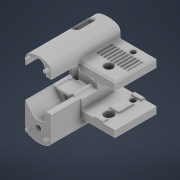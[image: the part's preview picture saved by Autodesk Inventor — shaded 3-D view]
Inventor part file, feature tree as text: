
AUTODESK INVENTOR PART (.ipt)
format: ipt  version: 2022.1 (Build 261234000, 234)  size: 1,596,416 bytes
history: native  units: mm
features: projected_geometry x43, extrude x31, sketch x31, reference x20, chamfer x19, other x11, move_body x11, direct_edit x8, fillet x7, hole x5, plane x4, delete_face x4, mirror x1
ambient origin geometry x8: Origin, YZ Plane, XZ Plane, XY Plane, X Axis, Y Axis, Z Axis, Center Point
bodies: Volumenkörper1 (feature_tree)
feature tree (195):
  extrude  "Extrusion1"  Depth=20.0mm
  extrude  "Extrusion2"  Depth=25.0mm
  plane  "Arbeitsebene1"
  extrude  "Extrusion5"  Depth=20.0mm
  sketch  "Skizze5"  dims[d7=20.0mm d8=10.0mm]
  extrude  "Extrusion6"  Depth=10.0mm
  hole  "Bohrung1"  [1 undecoded]
  extrude  "Extrusion10"  Depth=7.1mm
  sketch  "Skizze10"  dims[d28=15.0mm d29=17.0mm]
  hole  "Bohrung2"  [1 undecoded]
  hole  "Bohrung3"  [1 undecoded]
  extrude  "Extrusion11"  Depth=0.1mm
  extrude  "Extrusion12"  Depth=7.1mm
  direct_edit  "Direktbearbeitung3"
  direct_edit  "Direktbearbeitung4"
  extrude  "Extrusion13"  Depth=7.1mm
  fillet  "Rundung6"  Radius=18.2mm
  direct_edit  "Direktbearbeitung5"
  extrude  "Extrusion14"  Depth=11.0mm TaperAngle=0.0deg
  chamfer  "Fase2"  [1 undecoded]
  chamfer  "Fase3"  [1 undecoded]
  hole  "Bohrung5"  [1 undecoded]
  extrude  "Extrusion18"  Depth=4.0mm TaperAngle=0.0deg
  chamfer  "Fase4"  Distance=11.0mm
  extrude  "Extrusion19"  TaperAngle=0.0deg  [1 undecoded]
  chamfer  "Fase5"  Distance=1.2mm
  plane  "Arbeitsebene2"
  mirror  "Spiegeln1"
  extrude  "Extrusion20"  Depth=1.2mm
  fillet  "Rundung7"  Radius=1.2mm
  extrude  "Extrusion21"  Depth=1.2mm
  chamfer  "Fase6"  Distance=1.2mm
  extrude  "Extrusion22"  Depth=0.6mm
  chamfer  "Fase7"  Distance=6.2mm
  fillet  "Rundung8"  Radius=2.269mm
  chamfer  "Fase8"  Distance=10.561825mm
  chamfer  "Fase9"  Distance=10.561825mm
  extrude  "Extrusion23"  Depth=0.6mm
  extrude  "Extrusion24"  Depth=0.6mm
  direct_edit  "Direktbearbeitung6"
  direct_edit  "Direktbearbeitung7"
  chamfer  "Fase10"  Distance=0.8mm
  chamfer  "Fase11"  Distance=0.8mm
  fillet  "Rundung11"  Radius=0.8mm
  sketch  "Skizze27"  dims[d66=5.2mm d67=6.0mm d68=4.0mm d69=2.0mm d70=90.0deg d71=8.0mm d72=0.0mm]
  extrude  "Extrusion25"  Depth=0.6mm
  extrude  "Extrusion26"  Depth=0.6mm
  plane  "Arbeitsebene4"
  hole  "Bohrung6"  [1 undecoded]
  chamfer  "Fase12"  Distance=0.8mm
  direct_edit  "Direktbearbeitung8"
  plane  "Arbeitsebene3"
  extrude  "Extrusion27"  Depth=0.6mm
  extrude  "Extrusion28"  Depth=0.6mm
  chamfer  "Fase14"  Distance=8.638175mm
  chamfer  "Fase15"  Angle=90.0deg  [1 undecoded]
  chamfer  "Fase16"  Distance=1.0mm
  extrude  "Extrusion29"  Depth=1.0mm TaperAngle=45.0deg
  delete_face  "Fläche löschen1"
  extrude  "Extrusion30"  Depth=1.0mm TaperAngle=45.0deg
  fillet  "Rundung15"  Radius=3.95mm
  extrude  "Extrusion31"  Depth=0.6mm
  delete_face  "Fläche löschen2"
  extrude  "Extrusion32"  Depth=7.1mm
  fillet  "Rundung18"  Radius=1.975mm
  chamfer  "Fase19"  Distance=2.225mm
  chamfer  "Fase20"  [1 undecoded]
  sketch  "Skizze36"  dims[d110=1.2mm]
  extrude  "Extrusion33"  Depth=0.6mm
  extrude  "Extrusion34"  Depth=0.6mm
  extrude  "Extrusion35"  Depth=0.6mm
  delete_face  "Fläche löschen3"
  chamfer  "Fase23"  Distance=2.8mm
  chamfer  "Fase24"  Distance=2.2mm
  direct_edit  "Direktbearbeitung11"
  direct_edit  "Direktbearbeitung12"
  extrude  "Extrusion36"  Depth=0.6mm
  fillet  "Rundung20"  Radius=3.6mm
  sketch  "Skizze42"  dims[d112=1.2mm]
  delete_face  "Fläche löschen6"
  extrude  "Extrusion40"  Depth=0.6mm
  extrude  "Extrusion41"  Depth=0.6mm
  chamfer  "Fase26"  Distance=4.95mm
  extrude  "Extrusion42"  Depth=0.5mm TaperAngle=45.0deg
  sketch  "Skizze1"  dims[d0=20.0mm d1=20.0mm]
  sketch  "Skizze2"  dims[d2=21.0mm d3=25.0mm]
  sketch  "Skizze4"  dims[d4=40.0mm d5=0.0mm d6=20.0mm]
  reference  "Referenz2"
  reference  "Referenz3"
  reference  "Referenz4"
  reference  "Referenz5"
  projected_geometry  "Projizierte Kontur2"
  sketch  "Skizze6"  dims[d9=0.0mm d10=0.0mm d11=-5.0mm]
  projected_geometry  "Projizierte Kontur3"
  sketch  "Skizze8"  dims[d25=7.1mm d26=7.1mm]
  reference  "Referenz6"
  reference  "Referenz7"
  projected_geometry  "Projizierte Kontur6"
  projected_geometry  "Projizierte Kontur7"
  reference  "Referenz9"
  sketch  "Skizze11"  dims[d30=1.0mm d31=18.0mm]
  projected_geometry  "Projizierte Kontur8"
  projected_geometry  "Projizierte Kontur9"
  sketch  "Skizze12"  dims[d32=18.2mm d33=0.1mm]
  projected_geometry  "Projizierte Kontur10"
  projected_geometry  "Projizierte Kontur11"
  sketch  "Skizze13"  dims[d34=36.0mm d35=0.0mm d36=7.1mm]
  projected_geometry  "Projizierte Kontur12"
  sketch  "Skizze14"  dims[d37=3.55mm d39=7.1mm d40=18.2mm]
  projected_geometry  "Projizierte Kontur13"
  projected_geometry  "Projizierte Kontur17"
  projected_geometry  "Projizierte Kontur18"
  sketch  "Skizze20"  dims[d41=9.1mm d42=11.0mm d43=0.0mm]
  projected_geometry  "Projizierte Kontur19"
  sketch  "Skizze21"  dims[d48=3.4mm d49=6.0mm d50=4.0mm d51=2.0mm d52=90.0deg d53=8.0mm d54=0.0mm d59=0.0mm d60=0.0mm]
  projected_geometry  "Projizierte Kontur20"
  sketch  "Skizze22"  dims[d61=40.0mm]
  projected_geometry  "Projizierte Kontur21"
  sketch  "Skizze23"  dims[d62=15.5mm]
  projected_geometry  "Projizierte Kontur22"
  sketch  "Skizze24"  dims[d63=10.0mm]
  projected_geometry  "Projizierte Kontur23"
  sketch  "Skizze25"  dims[d64=6.2385mm]
  reference  "Referenz12"
  reference  "Referenz13"
  reference  "Referenz14"
  reference  "Referenz15"
  sketch  "Skizze26"  dims[d65=14.53mm]
  projected_geometry  "Projizierte Kontur24"
  projected_geometry  "Projizierte Kontur25"
  projected_geometry  "Projizierte Kontur26"
  projected_geometry  "Projizierte Kontur27"
  projected_geometry  "Projizierte Kontur28"
  sketch  "Skizze28"  dims[d73=3.2mm d74=6.0mm d75=4.0mm d76=2.0mm d77=90.0deg d78=8.0mm d79=0.0mm d80=0.0mm d81=0.0mm]
  sketch  "Skizze29"  dims[d82=11.0mm d83=0.0mm d87=0.0mm d88=0.0mm d89=4.0mm]
  projected_geometry  "Projizierte Kontur29"
  sketch  "Skizze30"  dims[d90=0.0mm d91=0.0mm d92=4.0mm d93=0.0mm d94=0.0mm d95=4.0mm]
  projected_geometry  "Projizierte Kontur30"
  projected_geometry  "Projizierte Kontur31"
  reference  "Referenz18"
  sketch  "Skizze31"  dims[d101=40.0mm]
  projected_geometry  "Projizierte Kontur32"
  projected_geometry  "Projizierte Kontur33"
  projected_geometry  "Projizierte Kontur34"
  sketch  "Skizze32"  dims[d102=20.0mm d103=11.0mm d104=0.0mm]
  projected_geometry  "Projizierte Kontur35"
  sketch  "Skizze33"  dims[d105=4.0mm d106=0.0mm d107=0.0mm d108=-5.0mm]
  projected_geometry  "Projizierte Kontur36"
  projected_geometry  "Projizierte Kontur37"
  sketch  "Skizze34"  dims[d109=9.4mm]
  projected_geometry  "Projizierte Kontur38"
  projected_geometry  "Projizierte Kontur39"
  reference  "Referenz20"
  projected_geometry  "Projizierte Kontur40"
  projected_geometry  "Projizierte Kontur41"
  sketch  "Skizze37"  dims[d111=1.2mm]
  reference  "Referenz21"
  reference  "Referenz22"
  reference  "Referenz23"
  reference  "Referenz24"
  reference  "Referenz25"
  reference  "Referenz26"
  reference  "Referenz27"
  sketch  "Skizze43"  dims[d113=1.2mm]
  projected_geometry  "Projizierte Kontur51"
  projected_geometry  "Projizierte Kontur52"
  projected_geometry  "Projizierte Kontur53"
  projected_geometry  "Projizierte Kontur54"
  projected_geometry  "Projizierte Kontur55"
  projected_geometry  "Projizierte Kontur56"
  projected_geometry  "Projizierte Kontur57"
  projected_geometry  "Projizierte Kontur58"
  sketch  "Skizze44"  dims[d114=1.2mm d115=1.2mm d116=1.2mm d117=1.2mm d118=1.2mm d119=1.2mm d121=6.2mm d122=6.2mm d123=2.269mm d124=10.561825mm d125=10.561825mm d126=0.8mm d127=0.8mm d128=0.8mm d129=0.8mm d130=0.8mm d131=0.8mm d132=0.8mm d133=0.8mm d134=0.8mm d135=14.53mm d136=6.2385mm d137=8.638175mm d138=90.0deg d139=1.0mm d140=0.0mm d141=1.0mm d142=2.0mm d143=45.0deg d146=1.0mm d147=2.0mm d148=45.0deg d160=3.95mm d161=4.45mm d162=7.1mm d163=1.975mm d164=2.225mm d165=0.0mm d166=3.55mm d169=2.8mm d170=2.8mm d171=2.8mm d172=2.2mm d173=2.8mm d174=6.0mm d175=3.05mm d176=2.0mm d177=8.726646mm d178=7.2mm d179=0.0mm d180=2.0mm d181=3.6mm d182=2.0mm d183=3.6mm d184=4.95mm d185=0.0mm d186=0.5mm d187=2.0mm d188=45.0deg d189=5.8mm d190=25.0mm d191=12.5mm d192=0.0mm d193=1.0mm d194=0.0mm d195=1.0mm d196=2.0mm d197=45.0deg d198=5.0mm d199=0.0mm d200=0.0mm d201=1.0mm d202=1.0mm d203=0.0mm d204=1.0mm d205=2.0mm d206=45.0deg d207=135.0deg d208=0.0mm d209=0.0mm d210=1.0mm d211=2.0mm d212=45.0deg d213=5.0mm d214=1.0mm d215=2.0mm d216=45.0deg d217=0.7071mm d218=2.0mm d219=45.0deg d220=4.0mm d221=11.1mm d222=1.38mm d223=9.0mm d224=1.31mm d225=1.31mm d226=1.05mm d227=1.648525mm d228=1.0mm d229=0.0mm d230=0.0mm d231=6.5mm d232=0.0mm d233=0.0mm d234=0.0mm d235=1.0mm d236=0.0mm d237=0.0mm d238=6.0mm d239=0.6mm d240=2.0mm d241=45.0deg d242=0.6mm d243=2.0mm d244=45.0deg d247=0.5mm d248=0.01mm d249=0.01mm d250=0.07mm d251=0.07mm d252=0.1mm d253=0.1mm d254=10.0mm d255=0.0mm d256=10.0mm d257=0.0mm d259=3.3mm d260=6.0mm d261=6.5mm d262=3.4mm d263=90.0deg d264=10.1mm d265=0.0mm d266=0.4mm d267=2.0mm d268=45.0deg d269=0.0mm d270=0.0mm d271=0.5mm d273=7.24mm d274=5.8mm d275=0.72mm d276=6.8mm d279=1.0mm d280=5.8mm d281=2.0mm d282=19.02mm d283=0.0mm d288=5.0mm d289=0.0mm d290=0.0mm d291=1.0mm d292=2.0mm d293=45.0deg d294=1.0mm d295=2.0mm d296=45.0deg d297=3.0mm d298=2.0mm d299=45.0deg d300=9.71mm d301=0.0mm d302=0.0mm d303=0.0mm d304=1.0mm d305=2.0mm d306=0.0mm d315=2.0mm d316=2.0mm d317=2.0mm d318=0.0mm d319=0.4mm d339=0.4mm d340=2.0mm d341=45.0deg d342=0.4mm d343=2.0mm d344=45.0deg d345=8.6mm d346=0.1mm d348=0.1mm d349=0.1mm d350=0.1mm d351=0.1mm d352=24.0mm d353=12.0mm d354=4.2mm d355=0.0mm d356=0.0mm d357=10.0mm d358=0.0mm d359=1.8mm d360=10.0mm d361=0.0mm d368=0.4mm d369=2.0mm d370=45.0deg d371=0.4mm d372=2.0mm d373=45.0deg d374=0.0mm d375=0.0mm d376=-3.0mm d377=0.0mm d378=0.0mm d379=-3.0mm d380=0.0mm d381=0.0mm d382=-1.5mm d383=0.0mm d384=0.0mm d385=-2.5mm d386=4.7mm d387=3.828427mm d388=2.3mm d389=2.0mm d390=2.0mm d391=0.0mm d392=2.38mm d393=2.38mm d394=0.0mm d395=2.5mm d396=8.48mm d401=0.04mm d402=0.04mm d403=0.04mm d404=0.04mm d405=0.04mm d406=0.04mm d408=10.0mm d409=0.0mm d410=3.0mm d429=0.0mm d430=2.861mm d478=0.0mm d479=0.0mm d480=0.11295mm d481=0.106442mm d482=0.106442mm d483=0.11295mm d484=10.0mm d485=0.0mm d486=1.0mm d487=2.0mm d488=45.0deg d489=1.0mm d490=6.0mm d491=12.0mm d492=8.0mm d493=0.6mm d494=0.0mm]
  other  "<userpath>\Desktop\Voron-2-2.4r1\Custom\Front_Idlers\Baugruppe1.iam"
  other  "Baugruppe1.iam"
  other  "Inside-holder:1"
  move_body  "Verschieben3"
  move_body  "Verschieben4"
  move_body  "Verschieben5"
  move_body  "Verschieben6"
  other  "<userpath>\Desktop\Voron-2-2.4r1\CAD\VORON2_v2.4_Assembly_Step\VORON2 v2.4 Assembly.iam"
  other  "VORON2 v2.4 Assembly.iam"
  other  "Z Assembly:1"
  other  "Z Belts:1"
  other  "Z Belt:2"
  move_body  "Verschieben7"
  move_body  "Verschieben8"
  move_body  "Verschieben9"
  other  "<userpath>\Desktop\Voron-2-2.4r1\Custom\Front_Idlers\Assembly_Front-Idlers2.iam"
  other  "Assembly_Front-Idlers2.iam"
  other  "Cover1:1"
  move_body  "Verschieben16"
  move_body  "Verschieben17"
  move_body  "Verschieben18"
  move_body  "Verschieben19"
note: 10 required parameter values undecoded (feature->parameter linkage not recoverable at this tier; creation-order binding heuristic only, values carry confidence <= 0.55)
